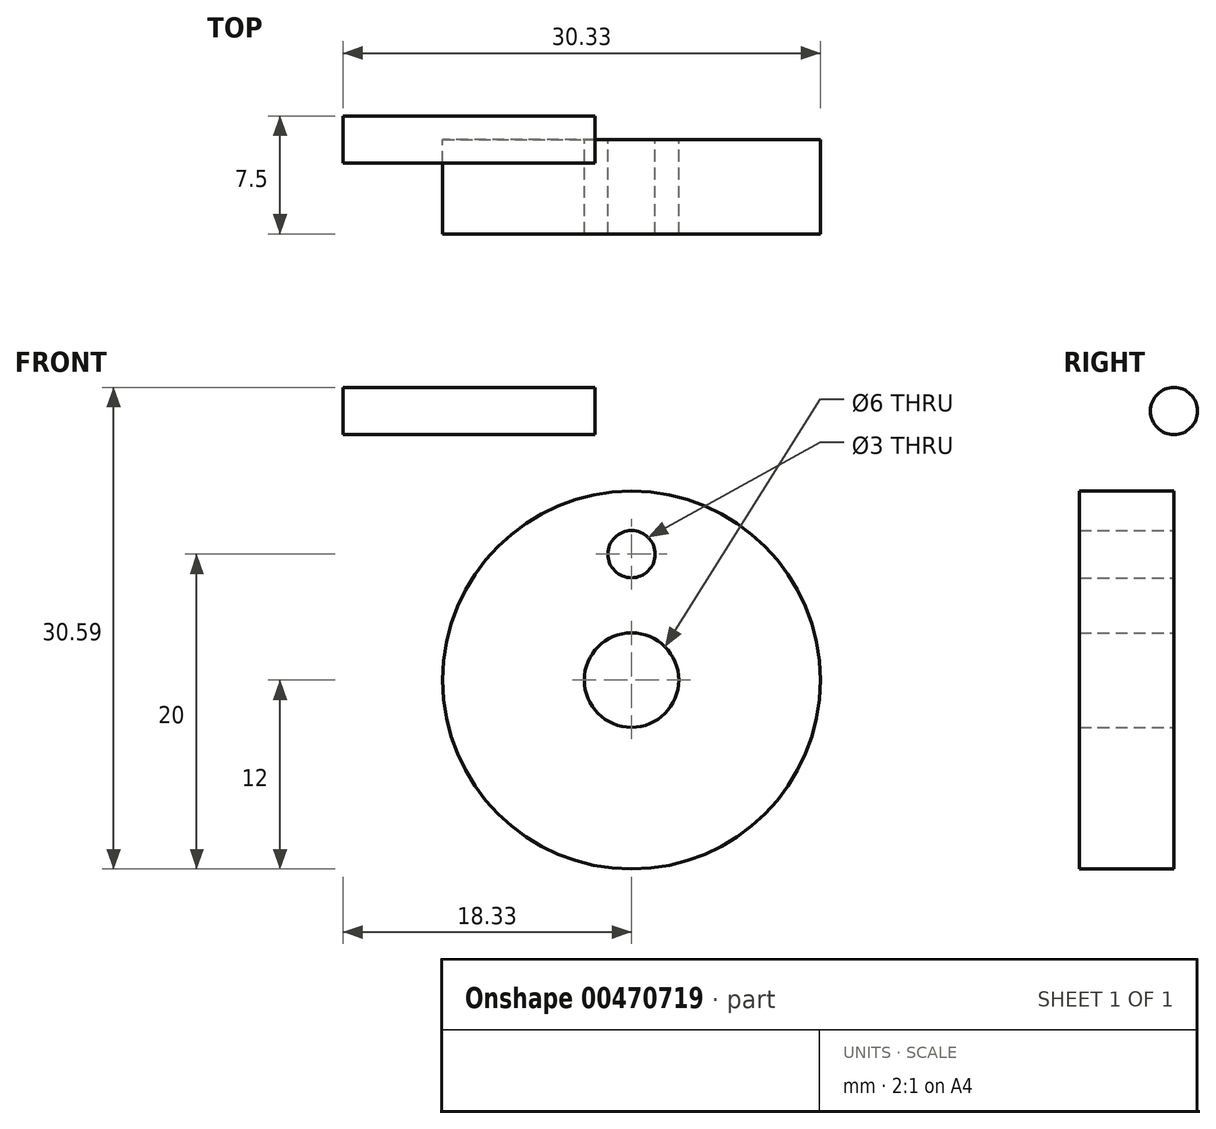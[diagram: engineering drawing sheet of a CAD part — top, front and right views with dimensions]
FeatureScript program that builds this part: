
annotation { "Feature Type Name" : "Feature", "Feature Type Description" : "" }
export const myFeature = defineFeature(function(context is Context, id is Id, definition is map)
    precondition{}
    {
        {
            var Q0;
            Q0=qCreatedBy(makeId("Front.planeOp"),FACE);
            var sketch = newSketch(context, id + "F0", { "sketchPlane" : qUnion([Q0])});
            skCircle(sketch, "E0", {"center": v(0, 0) * mm, "radius": 12 * mm});
            skCircle(sketch, "E1", {"center": v(0, 0) * mm, "radius": 3 * mm});
            skLineSegment(sketch, "E2", {"start": v(0, 0) * mm, "end": v(0, 8) * mm, "construction": true});
            skCircle(sketch, "E3", {"center": v(0, 8) * mm, "radius": 1.5 * mm});
            skLineSegment(sketch, "E4.bottom", {"start": v(-18.33, 18.6) * mm, "end": v(-2.33, 18.6) * mm});
            skLineSegment(sketch, "E4.top", {"start": v(-18.33, 17.1) * mm, "end": v(-2.33, 17.1) * mm});
            skLineSegment(sketch, "E4.left", {"start": v(-18.33, 18.6) * mm, "end": v(-18.33, 17.1) * mm});
            skLineSegment(sketch, "E4.right", {"start": v(-2.33, 18.6) * mm, "end": v(-2.33, 17.1) * mm});
            skSolve(sketch);
        }
        {
            var Q0;
            Q0=makeQuery(id+"F0.imprint","IMPRINT",FACE,{"disambiguationData":[TD([[makeQuery(id+"F0.imprint","IMPRINT",EDGE,{"derivedFrom":sQuery(id+"F0.wireOp",EDGE,"E0")}),1.0]])]});
            extrude(context, id + "F1", {"entities" : qUnion([Q0]), "depth" : 6 * mm});
        }
        {
            var Q0;
            Q0=makeQuery(id+"F0.imprint","IMPRINT",FACE,{"disambiguationData":[TD([[makeQuery(id+"F0.imprint","IMPRINT",EDGE,{"derivedFrom":sQuery(id+"F0.wireOp",EDGE,"E4.bottom")}),-1.0]])]});
            var Q1;
            Q1=sQuery(id+"F0.wireOp",EDGE,"E4.top");
            revolve(context, id + "F2", {"entities" : qUnion([Q0]), "axis" : qUnion([Q1]), "revolveType" : RevolveType.FULL});
        }
    });
